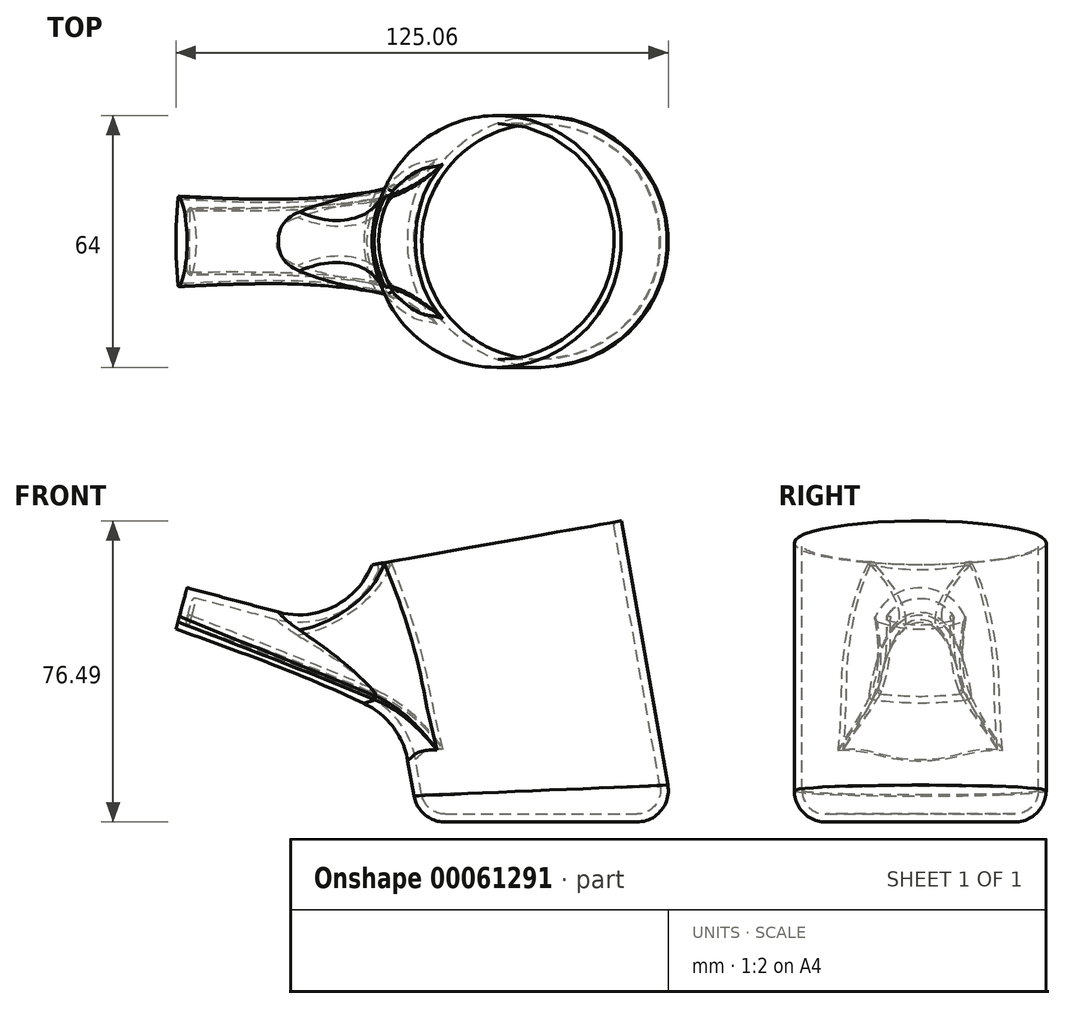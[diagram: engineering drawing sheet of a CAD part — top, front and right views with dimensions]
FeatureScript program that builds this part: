
annotation { "Feature Type Name" : "Feature", "Feature Type Description" : "" }
export const myFeature = defineFeature(function(context is Context, id is Id, definition is map)
    precondition{}
    {
        {
            assignVariable(context, id + "F0", {"name" : "F2", "anyValue" : 22});
        }
        {
            assignVariable(context, id + "F1", {"name" : "Sh", "anyValue" : 2});
        }
        {
            assignVariable(context, id + "F2", {"name" : "F5", "anyValue" : 8});
        }
        {
            assignVariable(context, id + "F3", {"name" : "F7", "anyValue" : getVariable(context, 'F5') - getVariable(context, 'Sh')});
        }
        {
            var Q0;
            Q0=qCreatedBy(makeId("Front.planeOp"),FACE);
            var sketch = newSketch(context, id + "F4", { "sketchPlane" : qUnion([Q0])});
            skLineSegment(sketch, "E0", {"start": v(0, 0) * mm, "end": v(-12.16, 68.94) * mm});
            skSolve(sketch);
        }
        {
            var Q0;
            Q0=sQuery(id+"F4.wireOp",VERTEX,"E0.end");
            var Q1;
            Q1=sQuery(id+"F4.wireOp",EDGE,"E0");
            cPlane(context, id + "F5", {"entities" : qUnion([Q0, Q1]), "cplaneType" : CPlaneType.LINE_POINT, "offset" : 150 * mm, "width" : 150 * mm, "height" : 150 * mm});
        }
        {
            var Q0;
            Q0=qCreatedBy(id+"F5.planeOp",FACE);
            var sketch = newSketch(context, id + "F6", { "sketchPlane" : qUnion([Q0])});
            skCircle(sketch, "E1", {"center": v(0, 0) * mm, "radius": 30 * mm});
            skSolve(sketch);
        }
        {
            var Q0;
            Q0 = qSketchRegion(id + "F6", true);
            var Q1;
            Q1=qCreatedBy(makeId("Top.planeOp"),FACE);
            extrude(context, id + "F7", {"entities" : qUnion([Q0]), "endBound" : BoundingType.UP_TO_SURFACE, "oppositeDirection" : true, "endBoundEntityFace" : qUnion([Q1]), "depth" : 25 * mm});
        }
        {
            var Q0;
            Q0=qCreatedBy(makeId("Front.planeOp"),FACE);
            var sketch = newSketch(context, id + "F8", { "sketchPlane" : qUnion([Q0])});
            skLineSegment(sketch, "E2", {"start": v(-91.34, 48.3) * mm, "end": v(-4.4, 25) * mm});
            skPoint(sketch, "E3", {"position": v(-47.87, 36.65) * mm});
            skSolve(sketch);
        }
        {
            var Q0;
            Q0=sQuery(id+"F8.wireOp",EDGE,"E2");
            var Q1;
            Q1=sQuery(id+"F8.wireOp",VERTEX,"E2.start");
            cPlane(context, id + "F9", {"entities" : qUnion([Q0, Q1]), "cplaneType" : CPlaneType.LINE_POINT, "offset" : 150 * mm, "width" : 150 * mm, "height" : 150 * mm});
        }
        {
            var Q0;
            Q0=qCreatedBy(id+"F9.planeOp",FACE);
            var sketch = newSketch(context, id + "F10", { "sketchPlane" : qUnion([Q0])});
            skArc(sketch, "E4", {"start": v(-9, 24.39) * mm, "mid": v(0, 23) * mm, "end": v(9, 24.39) * mm});
            skArc(sketch, "E5", {"start": v(9, 24.39) * mm, "mid": v(0, 30.03) * mm, "end": v(-9, 24.39) * mm});
            skSolve(sketch);
        }
        {
            var Q0;
            Q0=sQuery(id+"F8.wireOp",VERTEX,"E2.end");
            var Q1;
            Q1=sQuery(id+"F8.wireOp",EDGE,"E2");
            cPlane(context, id + "F11", {"entities" : qUnion([Q0, Q1]), "cplaneType" : CPlaneType.LINE_POINT, "offset" : 150 * mm, "width" : 150 * mm, "height" : 150 * mm});
        }
        {
            var Q0;
            Q0=qCreatedBy(id+"F11.planeOp",FACE);
            var sketch = newSketch(context, id + "F12", { "sketchPlane" : qUnion([Q0])});
            skArc(sketch, "E6.0", {"start": v(-19.83, 12.61) * mm, "mid": v(0, 8) * mm, "end": v(19.83, 12.61) * mm});
            skArc(sketch, "E7", {"start": v(19.83, 12.61) * mm, "mid": v(0, 30.03) * mm, "end": v(-19.83, 12.61) * mm});
            skSolve(sketch);
        }
        {
            var Q0;
            Q0=sQuery(id+"F8.wireOp",VERTEX,"E3");
            var Q1;
            Q1=sQuery(id+"F8.wireOp",EDGE,"E2");
            cPlane(context, id + "F13", {"entities" : qUnion([Q0, Q1]), "cplaneType" : CPlaneType.LINE_POINT, "offset" : 150 * mm, "width" : 150 * mm, "height" : 150 * mm});
        }
        {
            var Q0;
            Q0=qCreatedBy(id+"F13.planeOp",FACE);
            var sketch = newSketch(context, id + "F14", { "sketchPlane" : qUnion([Q0])});
            skArc(sketch, "E8.0", {"start": v(-9.98, 19.46) * mm, "mid": v(0, 18) * mm, "end": v(9.98, 19.46) * mm});
            skArc(sketch, "E9", {"start": v(9.98, 19.46) * mm, "mid": v(0, 30.03) * mm, "end": v(-9.98, 19.46) * mm});
            skSolve(sketch);
        }
        {
            var Q1;
            Q1=makeQuery(id+"F10.imprint","IMPRINT",FACE,{"disambiguationData":[TD([[makeQuery(id+"F10.imprint","IMPRINT",EDGE,{"derivedFrom":sQuery(id+"F10.wireOp",EDGE,"E4")}),1.0]])]});
            var Q2;
            Q2=makeQuery(id+"F14.imprint","IMPRINT",FACE,{"disambiguationData":[TD([[makeQuery(id+"F14.imprint","IMPRINT",EDGE,{"derivedFrom":sQuery(id+"F14.wireOp",EDGE,"E8.0")}),1.0]])]});
            var Q3;
            Q3=makeQuery(id+"F12.imprint","IMPRINT",FACE,{"disambiguationData":[TD([[makeQuery(id+"F12.imprint","IMPRINT",EDGE,{"derivedFrom":sQuery(id+"F12.wireOp",EDGE,"E6.0")}),1.0]])]});
            var Q4;
            Q4=sQuery(id+"F8.wireOp",EDGE,"E2");
            loft(context, id + "F15", {"operationType" : NewBodyOperationType.ADD, "sheetProfilesArray" : [{ "sheetProfileEntities" : qUnion([Q1]) }, { "sheetProfileEntities" : qUnion([Q2]) }, { "sheetProfileEntities" : qUnion([Q3]) }], "guidesArray" : [{ "guideEntities" : qUnion([Q4]), "guideDerivativeType" : LoftGuideDerivativeType.DEFAULT, "guideDerivativeMagnitude" : 1 }]});
        }
        {
            var Q0;
            {var subQ0=sQuery(id+"F14.wireOp",EDGE,"E8.0");var subQ1=sQuery(id+"F14.wireOp",EDGE,"E9");var subQ2=sQuery(id+"F10.wireOp",EDGE,"E4");var subQ3=sQuery(id+"F10.wireOp",EDGE,"E5");Q0=makeQuery(id+"F15.boolean.opBoolean","INTERSECT",EDGE,{"derivedFrom":[makeQuery(id+"F7.opExtrude","SWEPT_FACE",FACE,{"disambiguationData":[OSD([sQuery(id+"F6.wireOp",EDGE,"E1")])]}),makeQuery(id+"F15.opLoft","SWEPT_FACE",FACE,{"disambiguationData":[OSD([subQ2,subQ3,subQ0,subQ1]),TDD([makeQuery(id+"F10.imprint","INTERSECT",VERTEX,{"disambiguationData":[OD(0.0)],"derivedFrom":[subQ2,subQ3]}),makeQuery(id+"F10.imprint","INTERSECT",VERTEX,{"disambiguationData":[OD(1.0)],"derivedFrom":[subQ2,subQ3]}),makeQuery(id+"F10.imprint","IMPRINT",EDGE,{"derivedFrom":subQ2}),makeQuery(id+"F14.imprint","INTERSECT",VERTEX,{"disambiguationData":[OD(0.0)],"derivedFrom":[subQ0,subQ1]}),makeQuery(id+"F14.imprint","INTERSECT",VERTEX,{"disambiguationData":[OD(1.0)],"derivedFrom":[subQ0,subQ1]}),makeQuery(id+"F14.imprint","IMPRINT",EDGE,{"derivedFrom":subQ0})])]})]});}
            var Q1;
            {var subQ0=sQuery(id+"F14.wireOp",EDGE,"E9");var subQ1=sQuery(id+"F14.wireOp",EDGE,"E8.0");var subQ2=sQuery(id+"F10.wireOp",EDGE,"E5");var subQ3=sQuery(id+"F10.wireOp",EDGE,"E4");Q1=makeQuery(id+"F15.boolean.opBoolean","INTERSECT",EDGE,{"derivedFrom":[makeQuery(id+"F7.opExtrude","SWEPT_FACE",FACE,{"disambiguationData":[OSD([sQuery(id+"F6.wireOp",EDGE,"E1")])]}),makeQuery(id+"F15.opLoft","SWEPT_FACE",FACE,{"disambiguationData":[OSD([subQ3,subQ2,subQ1,subQ0]),TDD([makeQuery(id+"F10.imprint","INTERSECT",VERTEX,{"disambiguationData":[OD(0.0)],"derivedFrom":[subQ3,subQ2]}),makeQuery(id+"F10.imprint","INTERSECT",VERTEX,{"disambiguationData":[OD(1.0)],"derivedFrom":[subQ3,subQ2]}),makeQuery(id+"F10.imprint","IMPRINT",EDGE,{"derivedFrom":subQ2}),makeQuery(id+"F14.imprint","INTERSECT",VERTEX,{"disambiguationData":[OD(0.0)],"derivedFrom":[subQ1,subQ0]}),makeQuery(id+"F14.imprint","INTERSECT",VERTEX,{"disambiguationData":[OD(1.0)],"derivedFrom":[subQ1,subQ0]}),makeQuery(id+"F14.imprint","IMPRINT",EDGE,{"derivedFrom":subQ0})])]})]});}
            fillet(context, id + "F16", {"entities" : qUnion([Q0, Q1]), "radius" : (getVariable(context, 'F2')) * mm, "tangentPropagation" : true, "allowEdgeOverflow" : false});
        }
        {
            var Q0;
            Q0=makeQuery(id+"F7.opExtrude","CAP_FACE",FACE,{"disambiguationData":[OSD([sQuery(id+"F6.wireOp",EDGE,"E1")])],"isStart":true});
            shell(context, id + "F17", {"entities" : qUnion([Q0]), "thickness" : (getVariable(context, 'Sh')) * mm, "oppositeDirection" : true});
        }
        {
            var Q0;
            {var subQ0=sQuery(id+"F14.wireOp",EDGE,"E9");var subQ1=sQuery(id+"F14.wireOp",EDGE,"E8.0");var subQ2=sQuery(id+"F10.wireOp",EDGE,"E5");var subQ3=sQuery(id+"F10.wireOp",EDGE,"E4");var subQ4=sQuery(id+"F6.wireOp",EDGE,"E1");Q0=makeQuery(id+"F17.opShell","OFFSET_FACE",FACE,{"disambiguationData":[OSD([subQ4,subQ3,subQ2,subQ1,subQ0]),TDD([makeQuery(id+"F16.opFillet","BLEND_FACE",FACE,{"disambiguationData":[OSD([subQ4,subQ3,subQ2,subQ1,subQ0]),TDD([makeQuery(id+"F15.boolean.opBoolean","INTERSECT",EDGE,{"derivedFrom":[makeQuery(id+"F7.opExtrude","SWEPT_FACE",FACE,{"disambiguationData":[OSD([subQ4])]}),makeQuery(id+"F15.opLoft","SWEPT_FACE",FACE,{"disambiguationData":[OSD([subQ3,subQ2,subQ1,subQ0]),TDD([makeQuery(id+"F10.imprint","INTERSECT",VERTEX,{"disambiguationData":[OD(0.0)],"derivedFrom":[subQ3,subQ2]}),makeQuery(id+"F10.imprint","INTERSECT",VERTEX,{"disambiguationData":[OD(1.0)],"derivedFrom":[subQ3,subQ2]}),makeQuery(id+"F10.imprint","IMPRINT",EDGE,{"derivedFrom":subQ2}),makeQuery(id+"F14.imprint","INTERSECT",VERTEX,{"disambiguationData":[OD(0.0)],"derivedFrom":[subQ1,subQ0]}),makeQuery(id+"F14.imprint","INTERSECT",VERTEX,{"disambiguationData":[OD(1.0)],"derivedFrom":[subQ1,subQ0]}),makeQuery(id+"F14.imprint","IMPRINT",EDGE,{"derivedFrom":subQ0})])]})]})])]})])]});}
            var Q1;
            {var subQ0=sQuery(id+"F14.wireOp",EDGE,"E8.0");var subQ1=sQuery(id+"F14.wireOp",EDGE,"E9");var subQ2=sQuery(id+"F10.wireOp",EDGE,"E4");var subQ3=sQuery(id+"F10.wireOp",EDGE,"E5");Q1=makeQuery(id+"F17.opShell","OFFSET_FACE",FACE,{"disambiguationData":[OSD([subQ2,subQ3,subQ0,subQ1]),TDD([makeQuery(id+"F15.opLoft","SWEPT_FACE",FACE,{"disambiguationData":[OSD([subQ2,subQ3,subQ0,subQ1]),TDD([makeQuery(id+"F10.imprint","INTERSECT",VERTEX,{"disambiguationData":[OD(0.0)],"derivedFrom":[subQ2,subQ3]}),makeQuery(id+"F10.imprint","INTERSECT",VERTEX,{"disambiguationData":[OD(1.0)],"derivedFrom":[subQ2,subQ3]}),makeQuery(id+"F10.imprint","IMPRINT",EDGE,{"derivedFrom":subQ2}),makeQuery(id+"F14.imprint","INTERSECT",VERTEX,{"disambiguationData":[OD(0.0)],"derivedFrom":[subQ0,subQ1]}),makeQuery(id+"F14.imprint","INTERSECT",VERTEX,{"disambiguationData":[OD(1.0)],"derivedFrom":[subQ0,subQ1]}),makeQuery(id+"F14.imprint","IMPRINT",EDGE,{"derivedFrom":subQ0})])]})])]});}
            fillet(context, id + "F18", {"entities" : qUnion([Q0, Q1]), "radius" : 1 * mm, "allowEdgeOverflow" : false});
        }
        {
            var Q0;
            {var subQ0=sQuery(id+"F14.wireOp",EDGE,"E9");var subQ1=sQuery(id+"F14.wireOp",EDGE,"E8.0");var subQ2=makeQuery(id+"F14.imprint","INTERSECT",VERTEX,{"disambiguationData":[OD(1.0)],"derivedFrom":[subQ1,subQ0]});var subQ3=makeQuery(id+"F14.imprint","INTERSECT",VERTEX,{"disambiguationData":[OD(0.0)],"derivedFrom":[subQ1,subQ0]});var subQ4=sQuery(id+"F10.wireOp",EDGE,"E5");var subQ5=sQuery(id+"F10.wireOp",EDGE,"E4");var subQ6=makeQuery(id+"F10.imprint","INTERSECT",VERTEX,{"disambiguationData":[OD(1.0)],"derivedFrom":[subQ5,subQ4]});var subQ7=makeQuery(id+"F10.imprint","INTERSECT",VERTEX,{"disambiguationData":[OD(0.0)],"derivedFrom":[subQ5,subQ4]});var subQ8=makeQuery(id+"F7.opExtrude","SWEPT_FACE",FACE,{"disambiguationData":[OSD([sQuery(id+"F6.wireOp",EDGE,"E1")])]});Q0=makeQuery(id+"F16.opFillet","BLEND_EDGE",EDGE,{"disambiguationData":[OD(1.0)],"blendedFrom":[makeQuery(id+"F15.boolean.opBoolean","INTERSECT",EDGE,{"derivedFrom":[subQ8,makeQuery(id+"F15.opLoft","SWEPT_FACE",FACE,{"disambiguationData":[OSD([subQ5,subQ4,subQ1,subQ0]),TDD([subQ7,subQ6,makeQuery(id+"F10.imprint","IMPRINT",EDGE,{"derivedFrom":subQ5}),subQ3,subQ2,makeQuery(id+"F14.imprint","IMPRINT",EDGE,{"derivedFrom":subQ1})])]})]}),makeQuery(id+"F15.boolean.opBoolean","INTERSECT",EDGE,{"derivedFrom":[subQ8,makeQuery(id+"F15.opLoft","SWEPT_FACE",FACE,{"disambiguationData":[OSD([subQ5,subQ4,subQ1,subQ0]),TDD([subQ7,subQ6,makeQuery(id+"F10.imprint","IMPRINT",EDGE,{"derivedFrom":subQ4}),subQ3,subQ2,makeQuery(id+"F14.imprint","IMPRINT",EDGE,{"derivedFrom":subQ0})])]})]})],"blendedInto":[]});}
            var Q1;
            {var subQ0=sQuery(id+"F14.wireOp",EDGE,"E9");var subQ1=sQuery(id+"F14.wireOp",EDGE,"E8.0");var subQ2=sQuery(id+"F12.wireOp",EDGE,"E7");var subQ3=sQuery(id+"F12.wireOp",EDGE,"E6.0");Q1=makeQuery(id+"F15.opLoft","SWEPT_EDGE",EDGE,{"disambiguationData":[OSD([subQ3,subQ2,subQ1,subQ0]),TDD([makeQuery(id+"F12.imprint","INTERSECT",VERTEX,{"disambiguationData":[OD(1.0)],"derivedFrom":[subQ3,subQ2]}),makeQuery(id+"F14.imprint","INTERSECT",VERTEX,{"disambiguationData":[OD(1.0)],"derivedFrom":[subQ1,subQ0]})])]});}
            var Q2;
            {var subQ0=sQuery(id+"F14.wireOp",EDGE,"E8.0");var subQ1=sQuery(id+"F14.wireOp",EDGE,"E9");var subQ2=makeQuery(id+"F14.imprint","INTERSECT",VERTEX,{"disambiguationData":[OD(1.0)],"derivedFrom":[subQ0,subQ1]});var subQ3=makeQuery(id+"F14.imprint","INTERSECT",VERTEX,{"disambiguationData":[OD(0.0)],"derivedFrom":[subQ0,subQ1]});var subQ4=sQuery(id+"F10.wireOp",EDGE,"E4");var subQ5=sQuery(id+"F10.wireOp",EDGE,"E5");var subQ6=makeQuery(id+"F10.imprint","INTERSECT",VERTEX,{"disambiguationData":[OD(1.0)],"derivedFrom":[subQ4,subQ5]});var subQ7=makeQuery(id+"F10.imprint","INTERSECT",VERTEX,{"disambiguationData":[OD(0.0)],"derivedFrom":[subQ4,subQ5]});Q2=makeQuery(id+"F16.opFillet","BLEND_EDGE",EDGE,{"disambiguationData":[OD(1.0)],"blendedFrom":[makeQuery(id+"F15.boolean.opBoolean","INTERSECT",EDGE,{"derivedFrom":[makeQuery(id+"F7.opExtrude","SWEPT_FACE",FACE,{"disambiguationData":[OSD([sQuery(id+"F6.wireOp",EDGE,"E1")])]}),makeQuery(id+"F15.opLoft","SWEPT_FACE",FACE,{"disambiguationData":[OSD([subQ4,subQ5,subQ0,subQ1]),TDD([subQ7,subQ6,makeQuery(id+"F10.imprint","IMPRINT",EDGE,{"derivedFrom":subQ5}),subQ3,subQ2,makeQuery(id+"F14.imprint","IMPRINT",EDGE,{"derivedFrom":subQ1})])]})]}),makeQuery(id+"F15.opLoft","SWEPT_FACE",FACE,{"disambiguationData":[OSD([subQ4,subQ5,subQ0,subQ1]),TDD([subQ7,subQ6,makeQuery(id+"F10.imprint","IMPRINT",EDGE,{"derivedFrom":subQ4}),subQ3,subQ2,makeQuery(id+"F14.imprint","IMPRINT",EDGE,{"derivedFrom":subQ0})])]})],"blendedInto":[makeQuery(id+"F15.opLoft","SWEPT_FACE",FACE,{"disambiguationData":[OSD([subQ4,subQ5,subQ0,subQ1]),TDD([subQ7,subQ6,makeQuery(id+"F10.imprint","IMPRINT",EDGE,{"derivedFrom":subQ4}),subQ3,subQ2,makeQuery(id+"F14.imprint","IMPRINT",EDGE,{"derivedFrom":subQ0})])]})]});}
            var Q3;
            {var subQ0=sQuery(id+"F14.wireOp",EDGE,"E9");var subQ1=sQuery(id+"F14.wireOp",EDGE,"E8.0");var subQ2=sQuery(id+"F10.wireOp",EDGE,"E5");var subQ3=sQuery(id+"F10.wireOp",EDGE,"E4");Q3=makeQuery(id+"F15.opLoft","SWEPT_EDGE",EDGE,{"disambiguationData":[OSD([subQ3,subQ2,subQ1,subQ0]),TDD([makeQuery(id+"F10.imprint","INTERSECT",VERTEX,{"disambiguationData":[OD(1.0)],"derivedFrom":[subQ3,subQ2]}),makeQuery(id+"F14.imprint","INTERSECT",VERTEX,{"disambiguationData":[OD(1.0)],"derivedFrom":[subQ1,subQ0]})])]});}
            var Q4;
            {var subQ0=sQuery(id+"F14.wireOp",EDGE,"E9");var subQ1=sQuery(id+"F14.wireOp",EDGE,"E8.0");var subQ2=makeQuery(id+"F14.imprint","INTERSECT",VERTEX,{"disambiguationData":[OD(1.0)],"derivedFrom":[subQ1,subQ0]});var subQ3=makeQuery(id+"F14.imprint","INTERSECT",VERTEX,{"disambiguationData":[OD(0.0)],"derivedFrom":[subQ1,subQ0]});var subQ4=sQuery(id+"F10.wireOp",EDGE,"E5");var subQ5=sQuery(id+"F10.wireOp",EDGE,"E4");var subQ6=makeQuery(id+"F10.imprint","INTERSECT",VERTEX,{"disambiguationData":[OD(1.0)],"derivedFrom":[subQ5,subQ4]});var subQ7=makeQuery(id+"F10.imprint","INTERSECT",VERTEX,{"disambiguationData":[OD(0.0)],"derivedFrom":[subQ5,subQ4]});var subQ8=makeQuery(id+"F7.opExtrude","SWEPT_FACE",FACE,{"disambiguationData":[OSD([sQuery(id+"F6.wireOp",EDGE,"E1")])]});Q4=makeQuery(id+"F16.opFillet","BLEND_EDGE",EDGE,{"disambiguationData":[OD(0.0)],"blendedFrom":[makeQuery(id+"F15.boolean.opBoolean","INTERSECT",EDGE,{"derivedFrom":[subQ8,makeQuery(id+"F15.opLoft","SWEPT_FACE",FACE,{"disambiguationData":[OSD([subQ5,subQ4,subQ1,subQ0]),TDD([subQ7,subQ6,makeQuery(id+"F10.imprint","IMPRINT",EDGE,{"derivedFrom":subQ5}),subQ3,subQ2,makeQuery(id+"F14.imprint","IMPRINT",EDGE,{"derivedFrom":subQ1})])]})]}),makeQuery(id+"F15.boolean.opBoolean","INTERSECT",EDGE,{"derivedFrom":[subQ8,makeQuery(id+"F15.opLoft","SWEPT_FACE",FACE,{"disambiguationData":[OSD([subQ5,subQ4,subQ1,subQ0]),TDD([subQ7,subQ6,makeQuery(id+"F10.imprint","IMPRINT",EDGE,{"derivedFrom":subQ4}),subQ3,subQ2,makeQuery(id+"F14.imprint","IMPRINT",EDGE,{"derivedFrom":subQ0})])]})]})],"blendedInto":[]});}
            fillet(context, id + "F19", {"entities" : qUnion([Q0, Q1, Q2, Q3, Q4]), "radius" : 1 * mm, "tangentPropagation" : true, "allowEdgeOverflow" : false});
        }
        {
            var Q0;
            {var subQ0=sQuery(id+"F6.wireOp",EDGE,"E1");Q0=makeQuery(id+"F17.opShell","OFFSET_EDGE",EDGE,{"disambiguationData":[OSD([subQ0]),TDD([makeQuery(id+"F7.opExtrude","CAP_EDGE",EDGE,{"disambiguationData":[OSD([subQ0])],"isStart":false})])]});}
            fillet(context, id + "F20", {"entities" : qUnion([Q0]), "radius" : (getVariable(context, 'F7')) * mm, "tangentPropagation" : true, "allowEdgeOverflow" : false});
        }
        {
            var Q0;
            Q0=makeQuery(id+"F7.opExtrude","CAP_EDGE",EDGE,{"disambiguationData":[OSD([sQuery(id+"F6.wireOp",EDGE,"E1")])],"isStart":false});
            fillet(context, id + "F21", {"entities" : qUnion([Q0]), "radius" : (getVariable(context, 'F5')) * mm, "tangentPropagation" : true, "allowEdgeOverflow" : false});
        }
        {
            var Q0;
            {var subQ0=sQuery(id+"F14.wireOp",EDGE,"E9");var subQ1=sQuery(id+"F14.wireOp",EDGE,"E8.0");var subQ2=sQuery(id+"F10.wireOp",EDGE,"E5");var subQ3=sQuery(id+"F10.wireOp",EDGE,"E4");Q0=makeQuery(id+"F17.opShell","OFFSET_FACE",FACE,{"disambiguationData":[OSD([subQ3,subQ2,subQ1,subQ0]),TDD([makeQuery(id+"F15.opLoft","SWEPT_FACE",FACE,{"disambiguationData":[OSD([subQ3,subQ2,subQ1,subQ0]),TDD([makeQuery(id+"F10.imprint","INTERSECT",VERTEX,{"disambiguationData":[OD(0.0)],"derivedFrom":[subQ3,subQ2]}),makeQuery(id+"F10.imprint","INTERSECT",VERTEX,{"disambiguationData":[OD(1.0)],"derivedFrom":[subQ3,subQ2]}),makeQuery(id+"F10.imprint","IMPRINT",EDGE,{"derivedFrom":subQ2}),makeQuery(id+"F14.imprint","INTERSECT",VERTEX,{"disambiguationData":[OD(0.0)],"derivedFrom":[subQ1,subQ0]}),makeQuery(id+"F14.imprint","INTERSECT",VERTEX,{"disambiguationData":[OD(1.0)],"derivedFrom":[subQ1,subQ0]}),makeQuery(id+"F14.imprint","IMPRINT",EDGE,{"derivedFrom":subQ0})])]})])]});}
            fillet(context, id + "F22", {"entities" : qUnion([Q0]), "radius" : 1 * mm, "tangentPropagation" : true, "allowEdgeOverflow" : false});
        }
    });
